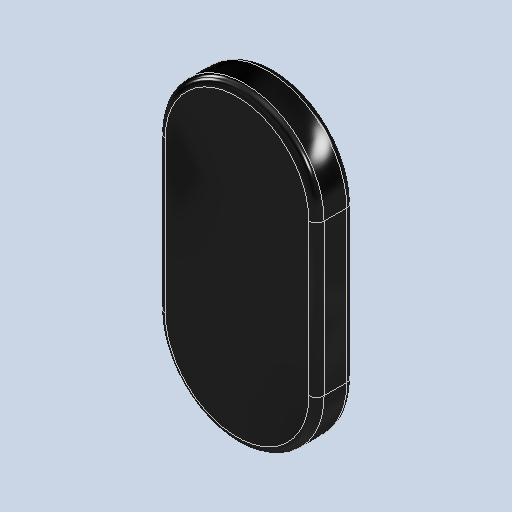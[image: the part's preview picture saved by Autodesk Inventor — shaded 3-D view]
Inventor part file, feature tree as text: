
AUTODESK INVENTOR PART (.ipt)
format: ipt  version: 2023.1 (Build 271208000, 208)  size: 257,024 bytes
history: native  units: mm
features: other x3, extrude x1, fillet x1, sketch x1, reference x1
ambient origin geometry x8: Origin, YZ Plane, XZ Plane, XY Plane, X Axis, Y Axis, Z Axis, Center Point
bodies: Volumenkörper1 (feature_tree)
feature tree (7):
  extrude  "Extrusion1"  Depth=1.0mm TaperAngle=0.0deg
  fillet  "Rundung1"  Radius=0.2mm
  sketch  "Skizze1"  dims[d0=4.2mm d1=1.0mm d2=0.0mm d3=0.2mm]
  reference  "Referenz1"
  other  "<userpath>\Desktop\GitHub\Voron-2-Mods\Misc\ISDT C4 EVO\CAD\Isdt.iam"
  other  "Isdt.iam"
  other  "Housing:1"
